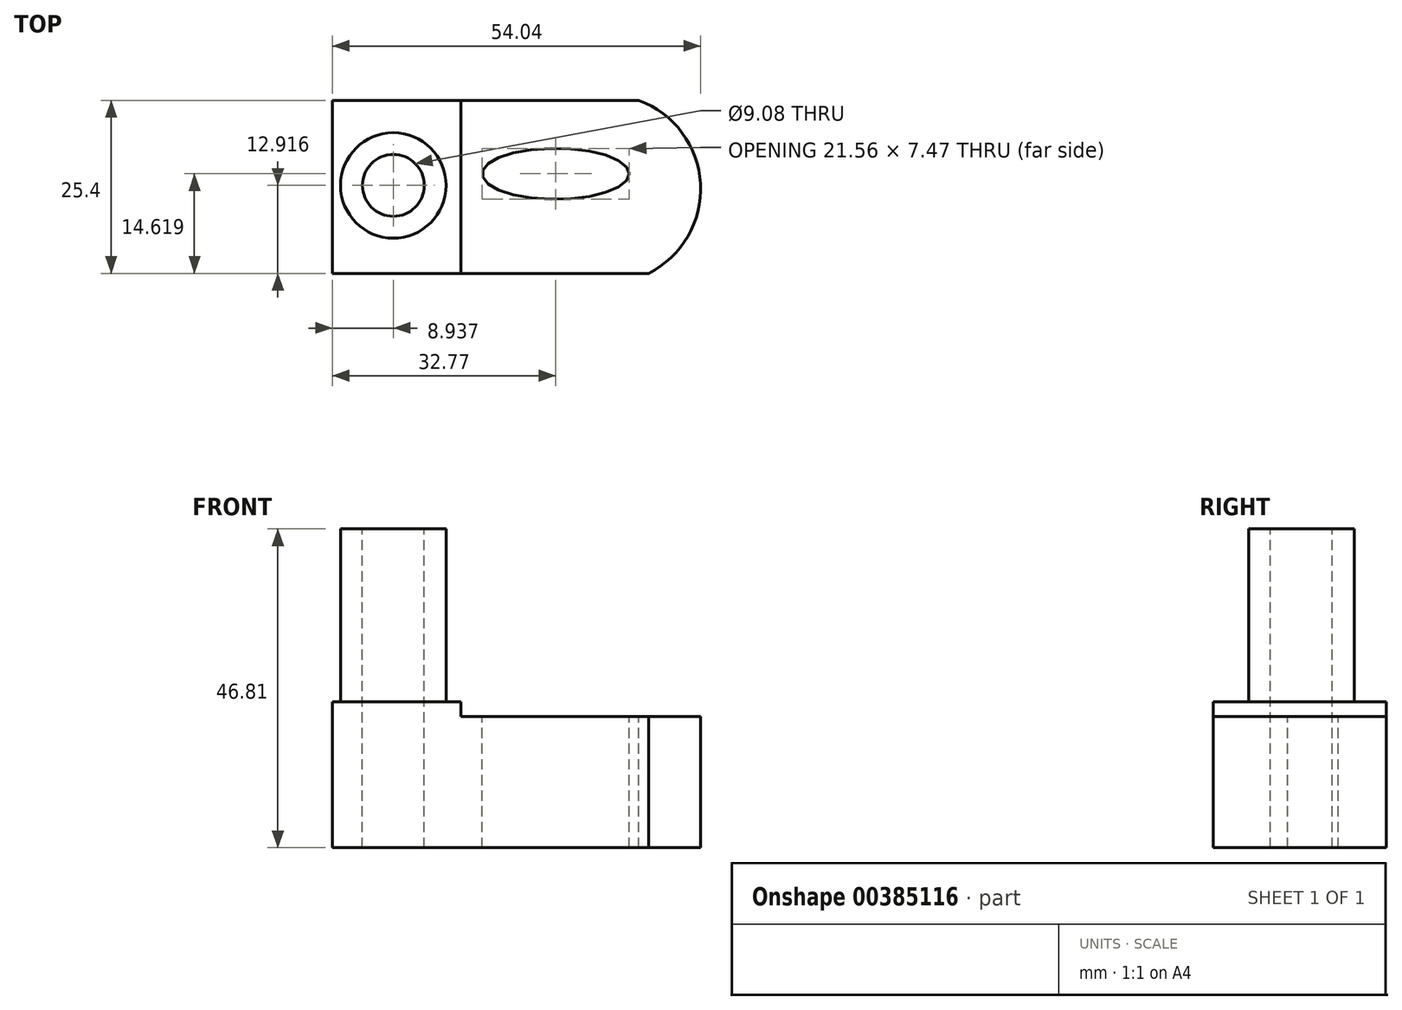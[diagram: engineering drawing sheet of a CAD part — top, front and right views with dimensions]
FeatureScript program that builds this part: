
annotation { "Feature Type Name" : "Feature", "Feature Type Description" : "" }
export const myFeature = defineFeature(function(context is Context, id is Id, definition is map)
    precondition{}
    {
        {
            var Q0;
            Q0=qCreatedBy(makeId("Front.planeOp"),FACE);
            var sketch = newSketch(context, id + "F0", { "sketchPlane" : qUnion([Q0])});
            skLineSegment(sketch, "E0", {"start": v(0, 0) * mm, "end": v(0, 46.81) * mm});
            skLineSegment(sketch, "E1", {"start": v(0, 46.81) * mm, "end": v(18.87, 46.81) * mm});
            skLineSegment(sketch, "E2", {"start": v(18.87, 46.81) * mm, "end": v(18.87, 19.3) * mm});
            skLineSegment(sketch, "E3", {"start": v(18.87, 19.3) * mm, "end": v(55.18, 19.3) * mm});
            skLineSegment(sketch, "E4", {"start": v(55.18, 19.3) * mm, "end": v(55.18, 0) * mm});
            skLineSegment(sketch, "E5", {"start": v(55.18, 0) * mm, "end": v(0, 0) * mm});
            skSolve(sketch);
        }
        {
            var Q0;
            Q0 = qSketchRegion(id + "F0", true);
            extrude(context, id + "F1", {"entities" : qUnion([Q0]), "depth" : 25.4 * mm});
        }
        {
            var Q0;
            Q0=makeQuery(id+"F1.opExtrude","SWEPT_FACE",FACE,{"disambiguationData":[OSD([sQuery(id+"F0.wireOp",EDGE,"E1")])]});
            var sketch = newSketch(context, id + "F2", { "sketchPlane" : qUnion([Q0])});
            skCircle(sketch, "E6", {"center": v(8.94, -12.48) * mm, "radius": 7.75 * mm});
            skSolve(sketch);
        }
        {
            var Q0;
            Q0=makeQuery(id+"F2.imprint","IMPRINT",FACE,{"disambiguationData":[TD([[makeQuery(id+"F2.imprint","IMPRINT",EDGE,{"derivedFrom":sQuery(id+"F2.wireOp",EDGE,"E6")}),-1.0]])]});
            extrude(context, id + "F3", {"entities" : qUnion([Q0]), "operationType" : NewBodyOperationType.REMOVE, "oppositeDirection" : true, "depth" : 25.4 * mm});
        }
        {
            var Q0;
            Q0=makeQuery(id+"F1.opExtrude","SWEPT_FACE",FACE,{"disambiguationData":[OSD([sQuery(id+"F0.wireOp",EDGE,"E3")])]});
            var sketch = newSketch(context, id + "F4", { "sketchPlane" : qUnion([Q0])});
            skArc(sketch, "E7", {"start": v(46.39, -25.4) * mm, "mid": v(54.02, -12.23) * mm, "end": v(44.97, 0) * mm});
            skSolve(sketch);
        }
        {
            var Q0;
            {var subQ0=sQuery(id+"F4.wireOp",EDGE,"E7");Q0=makeQuery(id+"F4.imprint","IMPRINT",FACE,{"disambiguationData":[TD([[makeQuery(id+"F4.imprint","IMPRINT",EDGE,{"derivedFrom":subQ0}),-1.0]])]});}
            extrude(context, id + "F5", {"entities" : qUnion([Q0]), "operationType" : NewBodyOperationType.REMOVE, "oppositeDirection" : true, "depth" : 25.4 * mm});
        }
        {
            var Q0;
            Q0=makeQuery(id+"F1.opExtrude","SWEPT_FACE",FACE,{"disambiguationData":[OSD([sQuery(id+"F0.wireOp",EDGE,"E3")])]});
            var sketch = newSketch(context, id + "F6", { "sketchPlane" : qUnion([Q0])});
            skEllipse(sketch, "E8", {"center": v(32.77, -10.78) * mm, "majorRadius": 10.78 * mm, "minorRadius": 3.74 * mm, "majorAxis": v(1, 0)});
            skSolve(sketch);
        }
        {
            var Q0;
            Q0=makeQuery(id+"F6.imprint","IMPRINT",FACE,{"disambiguationData":[TD([[makeQuery(id+"F6.imprint","IMPRINT",EDGE,{"derivedFrom":sQuery(id+"F6.wireOp",EDGE,"E8")}),1.0]])]});
            extrude(context, id + "F7", {"entities" : qUnion([Q0]), "operationType" : NewBodyOperationType.REMOVE, "oppositeDirection" : true, "depth" : 25.4 * mm});
        }
        {
            var Q0;
            Q0=makeQuery(id+"F1.opExtrude","SWEPT_FACE",FACE,{"disambiguationData":[OSD([sQuery(id+"F0.wireOp",EDGE,"E1")])]});
            var sketch = newSketch(context, id + "F8", { "sketchPlane" : qUnion([Q0])});
            skCircle(sketch, "E9", {"center": v(8.94, -12.48) * mm, "radius": 4.54 * mm});
            skSolve(sketch);
        }
        {
            var Q0;
            Q0=makeQuery(id+"F8.imprint","IMPRINT",FACE,{"disambiguationData":[TD([[makeQuery(id+"F8.imprint","IMPRINT",EDGE,{"derivedFrom":sQuery(id+"F8.wireOp",EDGE,"E9")}),1.0]])]});
            extrude(context, id + "F9", {"entities" : qUnion([Q0]), "operationType" : NewBodyOperationType.REMOVE, "oppositeDirection" : true, "depth" : 50.8 * mm});
        }
    });
